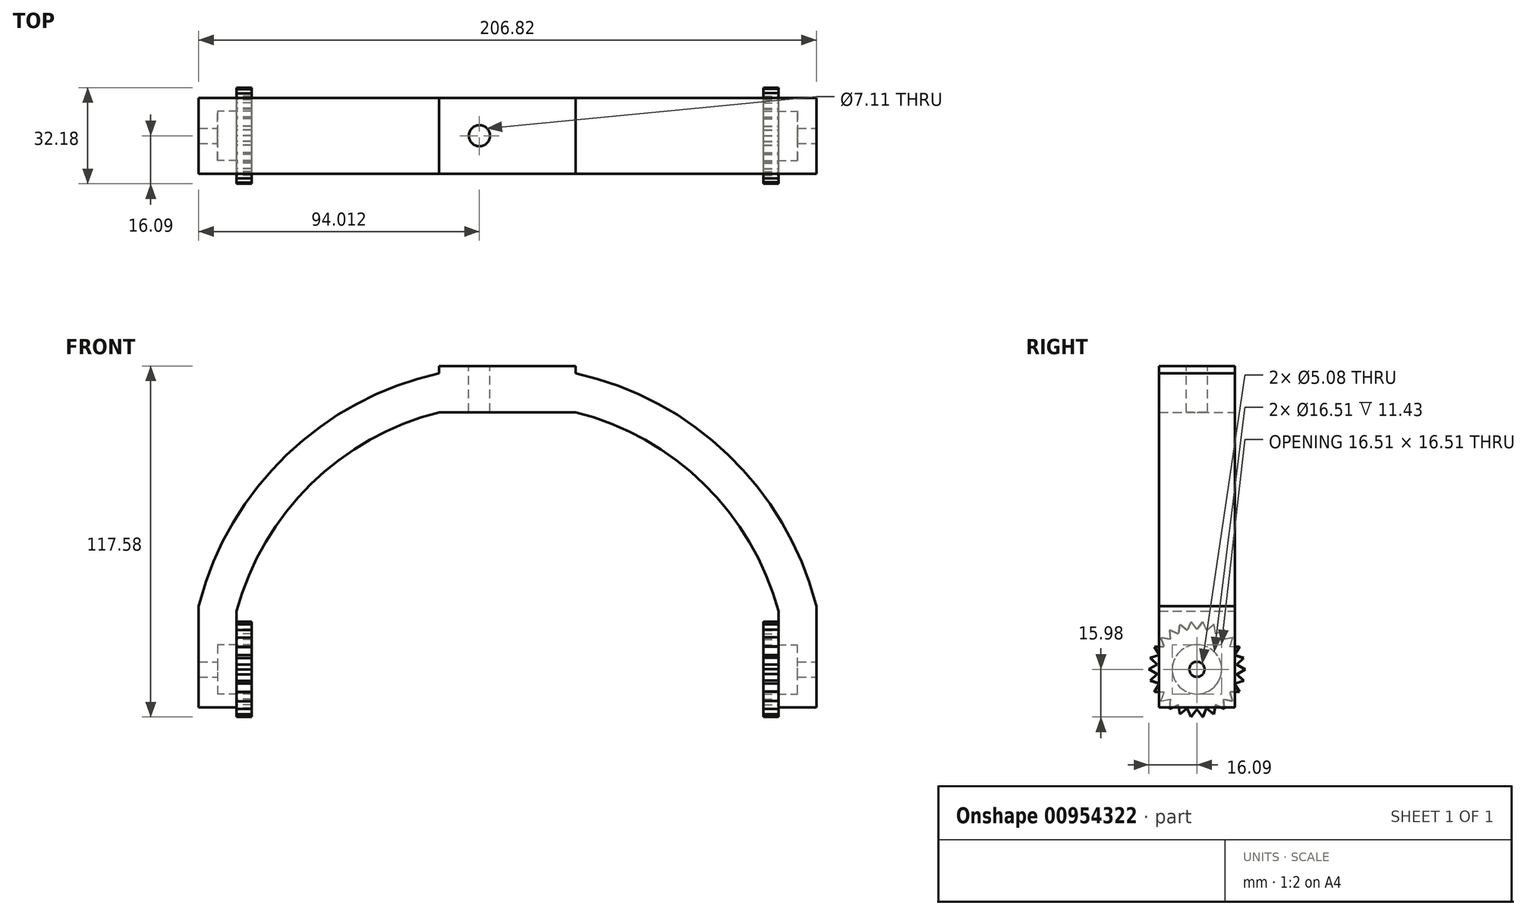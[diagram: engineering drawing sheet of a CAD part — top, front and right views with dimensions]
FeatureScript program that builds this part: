
annotation { "Feature Type Name" : "Feature", "Feature Type Description" : "" }
export const myFeature = defineFeature(function(context is Context, id is Id, definition is map)
    precondition{}
    {
        {
            var Q0;
            Q0=qCreatedBy(makeId("Front.planeOp"),FACE);
            var sketch = newSketch(context, id + "F0", { "sketchPlane" : qUnion([Q0])});
            skArc(sketch, "E0", {"start": v(97.06, 33.02) * mm, "mid": v(0, 107.95) * mm, "end": v(-97.06, 33.02) * mm});
            skLineSegment(sketch, "E1", {"start": v(-97.06, 33.02) * mm, "end": v(-97.06, 0) * mm});
            skLineSegment(sketch, "E2", {"start": v(97.06, 33.02) * mm, "end": v(97.06, 0) * mm});
            skSolve(sketch);
        }
        {
            var Q0;
            Q0=qCreatedBy(makeId("Top.planeOp"),FACE);
            var sketch = newSketch(context, id + "F1", { "sketchPlane" : qUnion([Q0])});
            skPoint(sketch, "E3.0", {"position": v(-97.06, 0) * mm});
            skLineSegment(sketch, "E4.bottom", {"start": v(-103.41, 12.7) * mm, "end": v(-90.71, 12.7) * mm});
            skLineSegment(sketch, "E4.top", {"start": v(-103.41, -12.7) * mm, "end": v(-90.71, -12.7) * mm});
            skLineSegment(sketch, "E4.left", {"start": v(-103.41, 12.7) * mm, "end": v(-103.41, -12.7) * mm});
            skLineSegment(sketch, "E4.right", {"start": v(-90.71, 12.7) * mm, "end": v(-90.71, -12.7) * mm});
            skSolve(sketch);
        }
        {
            var Q0;
            Q0=qSketchRegion(id+"F1",true);
            var Q1;
            Q1=qConstructionFilter(qBodyType(qCreatedBy(id+"F0",EDGE),BodyType.WIRE),ConstructionObject.NO);
            sweep(context, id + "F2", {"profiles" : qUnion([Q0]), "path" : qUnion([Q1])});
        }
        {
            var Q0;
            Q0=qCreatedBy(makeId("Right.planeOp"),FACE);
            var sketch = newSketch(context, id + "F3", { "sketchPlane" : qUnion([Q0])});
            skCircle(sketch, "E5", {"center": v(0, 12.7) * mm, "radius": 2.54 * mm});
            skSolve(sketch);
        }
        {
            var Q0;
            Q0=qSketchRegion(id+"F3",true);
            extrude(context, id + "F4", {"entities" : qUnion([Q0]), "operationType" : NewBodyOperationType.REMOVE, "endBound" : BoundingType.SYMMETRIC, "oppositeDirection" : true, "depth" : 254 * mm, "offsetDistance" : 25.4 * mm});
        }
        {
            var Q0;
            Q0=makeQuery(id+"F2.opSweep","SWEPT_FACE",FACE,{"disambiguationData":[OSD([sQuery(id+"F0.wireOp",EDGE,"E2"),sQuery(id+"F1.wireOp",EDGE,"E4.left")])]});
            var Q1;
            Q1=makeQuery(id+"F2.opSweep","CAP_VERTEX",VERTEX,{"disambiguationData":[OSD([sQuery(id+"F0.wireOp",EDGE,"E2"),sQuery(id+"F1.wireOp",EDGE,"E4.bottom"),sQuery(id+"F1.wireOp",EDGE,"E4.left")])],"isStart":false});
            cPlane(context, id + "F5", {"entities" : qUnion([Q0, Q1]), "cplaneType" : CPlaneType.PLANE_POINT, "offset" : 25.4 * mm, "width" : 152.4 * mm, "height" : 152.4 * mm});
        }
        {
            var Q0;
            Q0=qCreatedBy(id+"F5.planeOp",FACE);
            var sketch = newSketch(context, id + "F6", { "sketchPlane" : qUnion([Q0])});
            skCircle(sketch, "E6", {"center": v(0, 12.7) * mm, "radius": 5.33 * mm, "construction": true});
            skLineSegment(sketch, "E7.0", {"start": v(-2.67, 17.32) * mm, "end": v(2.67, 17.32) * mm});
            skLineSegment(sketch, "E7.1", {"start": v(2.67, 17.32) * mm, "end": v(5.33, 12.7) * mm});
            skLineSegment(sketch, "E7.2", {"start": v(5.33, 12.7) * mm, "end": v(2.67, 8.08) * mm});
            skLineSegment(sketch, "E7.3", {"start": v(2.67, 8.08) * mm, "end": v(-2.67, 8.08) * mm});
            skLineSegment(sketch, "E7.4", {"start": v(-2.67, 8.08) * mm, "end": v(-5.33, 12.7) * mm});
            skLineSegment(sketch, "E7.5", {"start": v(-5.33, 12.7) * mm, "end": v(-2.67, 17.32) * mm});
            skSolve(sketch);
        }
        {
            var Q0;
            Q0=makeQuery(id+"F2.opSweep","SWEPT_FACE",FACE,{"disambiguationData":[OSD([sQuery(id+"F0.wireOp",EDGE,"E1"),sQuery(id+"F1.wireOp",EDGE,"E4.left")])]});
            var Q1;
            Q1=makeQuery(id+"F2.opSweep","CAP_VERTEX",VERTEX,{"disambiguationData":[OSD([sQuery(id+"F0.wireOp",EDGE,"E1"),sQuery(id+"F1.wireOp",EDGE,"E4.bottom"),sQuery(id+"F1.wireOp",EDGE,"E4.left")])],"isStart":true});
            cPlane(context, id + "F7", {"entities" : qUnion([Q0, Q1]), "cplaneType" : CPlaneType.PLANE_POINT, "offset" : 25.4 * mm, "width" : 152.4 * mm, "height" : 152.4 * mm});
        }
        {
            var Q0;
            Q0=qCreatedBy(id+"F7.planeOp",FACE);
            var sketch = newSketch(context, id + "F8", { "sketchPlane" : qUnion([Q0])});
            skLineSegment(sketch, "E8", {"start": v(0, 0) * mm, "end": v(0, 12.7) * mm, "construction": true});
            skCircle(sketch, "E9", {"center": v(0, 12.7) * mm, "radius": 5.33 * mm, "construction": true});
            skLineSegment(sketch, "E10.0", {"start": v(-2.67, 17.32) * mm, "end": v(2.67, 17.32) * mm});
            skLineSegment(sketch, "E10.1", {"start": v(2.67, 17.32) * mm, "end": v(5.33, 12.7) * mm});
            skLineSegment(sketch, "E10.2", {"start": v(5.33, 12.7) * mm, "end": v(2.67, 8.08) * mm});
            skLineSegment(sketch, "E10.3", {"start": v(2.67, 8.08) * mm, "end": v(-2.67, 8.08) * mm});
            skLineSegment(sketch, "E10.4", {"start": v(-2.67, 8.08) * mm, "end": v(-5.33, 12.7) * mm});
            skLineSegment(sketch, "E10.5", {"start": v(-5.33, 12.7) * mm, "end": v(-2.67, 17.32) * mm});
            skSolve(sketch);
        }
        {
            var Q0;
            Q0=makeQuery(id+"F2.opSweep","SWEPT_FACE",FACE,{"disambiguationData":[OSD([sQuery(id+"F0.wireOp",EDGE,"E1"),sQuery(id+"F1.wireOp",EDGE,"E4.left")])]});
            cPlane(context, id + "F9", {"entities" : qUnion([Q0]), "cplaneType" : CPlaneType.OFFSET, "offset" : 6.35 * mm, "oppositeDirection" : true, "width" : 152.4 * mm, "height" : 152.4 * mm});
        }
        {
            var Q0;
            Q0=qCreatedBy(id+"F9.planeOp",FACE);
            var sketch = newSketch(context, id + "F10", { "sketchPlane" : qUnion([Q0])});
            skLineSegment(sketch, "E11", {"start": v(0, 0) * mm, "end": v(0, 12.7) * mm, "construction": true});
            skCircle(sketch, "E12", {"center": v(0, 12.7) * mm, "radius": 8.26 * mm});
            skSolve(sketch);
        }
        {
            var Q0;
            Q0=makeQuery(id+"F2.opSweep","SWEPT_FACE",FACE,{"disambiguationData":[OSD([sQuery(id+"F0.wireOp",EDGE,"E2"),sQuery(id+"F1.wireOp",EDGE,"E4.left")])]});
            cPlane(context, id + "F11", {"entities" : qUnion([Q0]), "cplaneType" : CPlaneType.OFFSET, "offset" : 6.35 * mm, "oppositeDirection" : true, "width" : 152.4 * mm, "height" : 152.4 * mm});
        }
        {
            var Q0;
            Q0=qCreatedBy(id+"F11.planeOp",FACE);
            var sketch = newSketch(context, id + "F12", { "sketchPlane" : qUnion([Q0])});
            skLineSegment(sketch, "E13", {"start": v(0, 0) * mm, "end": v(0, 12.7) * mm, "construction": true});
            skCircle(sketch, "E14", {"center": v(0, 12.7) * mm, "radius": 8.26 * mm});
            skSolve(sketch);
        }
        {
            var Q0;
            Q0=makeQuery(id+"F2.opSweep","SWEPT_FACE",FACE,{"disambiguationData":[OSD([sQuery(id+"F0.wireOp",EDGE,"E1"),sQuery(id+"F1.wireOp",EDGE,"E4.right")])]});
            var sketch = newSketch(context, id + "F13", { "sketchPlane" : qUnion([Q0])});
            skCircle(sketch, "E15", {"center": v(0, 12.7) * mm, "radius": 13.34 * mm, "construction": true});
            skLineSegment(sketch, "E16", {"start": v(-3.28, 25.63) * mm, "end": v(-2, 28.67) * mm});
            skLineSegment(sketch, "E17", {"start": v(-2, 28.67) * mm, "end": v(0, 26.04) * mm});
            skLineSegment(sketch, "E18.1.0", {"start": v(-6.27, 24.47) * mm, "end": v(-5.76, 27.73) * mm});
            skLineSegment(sketch, "E18.1.1", {"start": v(-5.76, 27.73) * mm, "end": v(-3.2, 25.65) * mm});
            skLineSegment(sketch, "E18.2.0", {"start": v(-8.9, 22.62) * mm, "end": v(-9.18, 25.91) * mm});
            skLineSegment(sketch, "E18.2.1", {"start": v(-9.18, 25.91) * mm, "end": v(-6.2, 24.5) * mm});
            skLineSegment(sketch, "E18.3.0", {"start": v(-11.02, 20.2) * mm, "end": v(-12.08, 23.33) * mm});
            skLineSegment(sketch, "E18.3.1", {"start": v(-12.08, 23.33) * mm, "end": v(-8.84, 22.68) * mm});
            skLineSegment(sketch, "E18.4.0", {"start": v(-12.5, 17.35) * mm, "end": v(-14.27, 20.13) * mm});
            skLineSegment(sketch, "E18.4.1", {"start": v(-14.27, 20.13) * mm, "end": v(-10.97, 20.28) * mm});
            skLineSegment(sketch, "E18.5.0", {"start": v(-13.25, 14.22) * mm, "end": v(-15.64, 16.5) * mm});
            skLineSegment(sketch, "E18.5.1", {"start": v(-15.64, 16.5) * mm, "end": v(-12.47, 17.43) * mm});
            skLineSegment(sketch, "E18.6.0", {"start": v(-13.23, 11) * mm, "end": v(-16.1, 12.65) * mm});
            skLineSegment(sketch, "E18.6.1", {"start": v(-16.1, 12.65) * mm, "end": v(-13.24, 14.3) * mm});
            skLineSegment(sketch, "E18.7.0", {"start": v(-12.44, 7.89) * mm, "end": v(-15.61, 8.8) * mm});
            skLineSegment(sketch, "E18.7.1", {"start": v(-15.61, 8.8) * mm, "end": v(-13.24, 11.1) * mm});
            skLineSegment(sketch, "E18.8.0", {"start": v(-10.92, 5.05) * mm, "end": v(-14.22, 5.17) * mm});
            skLineSegment(sketch, "E18.8.1", {"start": v(-14.22, 5.17) * mm, "end": v(-12.47, 7.97) * mm});
            skLineSegment(sketch, "E18.9.0", {"start": v(-8.78, 2.66) * mm, "end": v(-12, 1.99) * mm});
            skLineSegment(sketch, "E18.9.1", {"start": v(-12, 1.99) * mm, "end": v(-10.97, 5.12) * mm});
            skLineSegment(sketch, "E18.10.0", {"start": v(-6.12, 0.85) * mm, "end": v(-9.1, -0.57) * mm});
            skLineSegment(sketch, "E18.10.1", {"start": v(-9.1, -0.57) * mm, "end": v(-8.84, 2.72) * mm});
            skLineSegment(sketch, "E18.11.0", {"start": v(-3.1, -0.27) * mm, "end": v(-5.66, -2.37) * mm});
            skLineSegment(sketch, "E18.11.1", {"start": v(-5.66, -2.37) * mm, "end": v(-6.2, 0.9) * mm});
            skLineSegment(sketch, "E18.12.0", {"start": v(0.09, -0.63) * mm, "end": v(-1.89, -3.28) * mm});
            skLineSegment(sketch, "E18.12.1", {"start": v(-1.89, -3.28) * mm, "end": v(-3.2, -0.25) * mm});
            skLineSegment(sketch, "E18.13.0", {"start": v(3.28, -0.23) * mm, "end": v(2, -3.27) * mm});
            skLineSegment(sketch, "E18.13.1", {"start": v(2, -3.27) * mm, "end": v(0, -0.63) * mm});
            skLineSegment(sketch, "E18.14.0", {"start": v(6.27, 0.93) * mm, "end": v(5.76, -2.33) * mm});
            skLineSegment(sketch, "E18.14.1", {"start": v(5.76, -2.33) * mm, "end": v(3.2, -0.25) * mm});
            skLineSegment(sketch, "E18.15.0", {"start": v(8.9, 2.78) * mm, "end": v(9.18, -0.51) * mm});
            skLineSegment(sketch, "E18.15.1", {"start": v(9.18, -0.51) * mm, "end": v(6.2, 0.9) * mm});
            skLineSegment(sketch, "E18.16.0", {"start": v(11.02, 5.2) * mm, "end": v(12.08, 2.07) * mm});
            skLineSegment(sketch, "E18.16.1", {"start": v(12.08, 2.07) * mm, "end": v(8.84, 2.72) * mm});
            skLineSegment(sketch, "E18.17.0", {"start": v(12.5, 8.05) * mm, "end": v(14.27, 5.27) * mm});
            skLineSegment(sketch, "E18.17.1", {"start": v(14.27, 5.27) * mm, "end": v(10.97, 5.12) * mm});
            skLineSegment(sketch, "E18.18.0", {"start": v(13.25, 11.18) * mm, "end": v(15.64, 8.9) * mm});
            skLineSegment(sketch, "E18.18.1", {"start": v(15.64, 8.9) * mm, "end": v(12.47, 7.97) * mm});
            skLineSegment(sketch, "E18.19.0", {"start": v(13.23, 14.4) * mm, "end": v(16.1, 12.75) * mm});
            skLineSegment(sketch, "E18.19.1", {"start": v(16.1, 12.75) * mm, "end": v(13.24, 11.1) * mm});
            skLineSegment(sketch, "E18.20.0", {"start": v(12.44, 17.51) * mm, "end": v(15.61, 16.6) * mm});
            skLineSegment(sketch, "E18.20.1", {"start": v(15.61, 16.6) * mm, "end": v(13.24, 14.3) * mm});
            skLineSegment(sketch, "E18.21.0", {"start": v(10.92, 20.35) * mm, "end": v(14.22, 20.23) * mm});
            skLineSegment(sketch, "E18.21.1", {"start": v(14.22, 20.23) * mm, "end": v(12.47, 17.43) * mm});
            skLineSegment(sketch, "E18.22.0", {"start": v(8.78, 22.74) * mm, "end": v(12, 23.41) * mm});
            skLineSegment(sketch, "E18.22.1", {"start": v(12, 23.41) * mm, "end": v(10.97, 20.28) * mm});
            skLineSegment(sketch, "E18.23.0", {"start": v(6.12, 24.55) * mm, "end": v(9.1, 25.97) * mm});
            skLineSegment(sketch, "E18.23.1", {"start": v(9.1, 25.97) * mm, "end": v(8.84, 22.68) * mm});
            skLineSegment(sketch, "E18.24.0", {"start": v(3.1, 25.67) * mm, "end": v(5.66, 27.77) * mm});
            skLineSegment(sketch, "E18.24.1", {"start": v(5.66, 27.77) * mm, "end": v(6.2, 24.5) * mm});
            skLineSegment(sketch, "E18.25.0", {"start": v(-0.09, 26.03) * mm, "end": v(1.89, 28.68) * mm});
            skLineSegment(sketch, "E18.25.1", {"start": v(1.89, 28.68) * mm, "end": v(3.2, 25.65) * mm});
            skSolve(sketch);
        }
        {
            var Q0;
            Q0=qSketchRegion(id+"F13",true);
            extrude(context, id + "F14", {"entities" : qUnion([Q0]), "operationType" : NewBodyOperationType.ADD, "depth" : 5.08 * mm, "offsetDistance" : 25.4 * mm});
        }
        {
            var Q0;
            Q0=makeQuery(id+"F2.opSweep","SWEPT_FACE",FACE,{"disambiguationData":[OSD([sQuery(id+"F0.wireOp",EDGE,"E2"),sQuery(id+"F1.wireOp",EDGE,"E4.right")])]});
            var sketch = newSketch(context, id + "F15", { "sketchPlane" : qUnion([Q0])});
            skCircle(sketch, "E19", {"center": v(0, 12.7) * mm, "radius": 13.34 * mm, "construction": true});
            skLineSegment(sketch, "E20", {"start": v(-3.28, 25.63) * mm, "end": v(-2, 28.67) * mm});
            skLineSegment(sketch, "E21", {"start": v(-2, 28.67) * mm, "end": v(0, 26.04) * mm});
            skLineSegment(sketch, "E22.1.0", {"start": v(-5.76, 27.73) * mm, "end": v(-3.2, 25.65) * mm});
            skLineSegment(sketch, "E22.1.1", {"start": v(-6.27, 24.47) * mm, "end": v(-5.76, 27.73) * mm});
            skLineSegment(sketch, "E22.2.0", {"start": v(-9.18, 25.91) * mm, "end": v(-6.2, 24.5) * mm});
            skLineSegment(sketch, "E22.2.1", {"start": v(-8.9, 22.62) * mm, "end": v(-9.18, 25.91) * mm});
            skLineSegment(sketch, "E22.3.0", {"start": v(-12.08, 23.33) * mm, "end": v(-8.84, 22.68) * mm});
            skLineSegment(sketch, "E22.3.1", {"start": v(-11.02, 20.2) * mm, "end": v(-12.08, 23.33) * mm});
            skLineSegment(sketch, "E22.4.0", {"start": v(-14.27, 20.13) * mm, "end": v(-10.97, 20.28) * mm});
            skLineSegment(sketch, "E22.4.1", {"start": v(-12.5, 17.35) * mm, "end": v(-14.27, 20.13) * mm});
            skLineSegment(sketch, "E22.5.0", {"start": v(-15.64, 16.5) * mm, "end": v(-12.47, 17.43) * mm});
            skLineSegment(sketch, "E22.5.1", {"start": v(-13.25, 14.22) * mm, "end": v(-15.64, 16.5) * mm});
            skLineSegment(sketch, "E22.6.0", {"start": v(-16.1, 12.65) * mm, "end": v(-13.24, 14.3) * mm});
            skLineSegment(sketch, "E22.6.1", {"start": v(-13.23, 11) * mm, "end": v(-16.1, 12.65) * mm});
            skLineSegment(sketch, "E22.7.0", {"start": v(-15.61, 8.8) * mm, "end": v(-13.24, 11.1) * mm});
            skLineSegment(sketch, "E22.7.1", {"start": v(-12.44, 7.89) * mm, "end": v(-15.61, 8.8) * mm});
            skLineSegment(sketch, "E22.8.0", {"start": v(-14.22, 5.17) * mm, "end": v(-12.47, 7.97) * mm});
            skLineSegment(sketch, "E22.8.1", {"start": v(-10.92, 5.05) * mm, "end": v(-14.22, 5.17) * mm});
            skLineSegment(sketch, "E22.9.0", {"start": v(-12, 1.99) * mm, "end": v(-10.97, 5.12) * mm});
            skLineSegment(sketch, "E22.9.1", {"start": v(-8.78, 2.66) * mm, "end": v(-12, 1.99) * mm});
            skLineSegment(sketch, "E22.10.0", {"start": v(-9.1, -0.57) * mm, "end": v(-8.84, 2.72) * mm});
            skLineSegment(sketch, "E22.10.1", {"start": v(-6.12, 0.85) * mm, "end": v(-9.1, -0.57) * mm});
            skLineSegment(sketch, "E22.11.0", {"start": v(-5.66, -2.37) * mm, "end": v(-6.2, 0.9) * mm});
            skLineSegment(sketch, "E22.11.1", {"start": v(-3.1, -0.27) * mm, "end": v(-5.66, -2.37) * mm});
            skLineSegment(sketch, "E22.12.0", {"start": v(-1.89, -3.28) * mm, "end": v(-3.2, -0.25) * mm});
            skLineSegment(sketch, "E22.12.1", {"start": v(0.09, -0.63) * mm, "end": v(-1.89, -3.28) * mm});
            skLineSegment(sketch, "E22.13.0", {"start": v(2, -3.27) * mm, "end": v(0, -0.63) * mm});
            skLineSegment(sketch, "E22.13.1", {"start": v(3.28, -0.23) * mm, "end": v(2, -3.27) * mm});
            skLineSegment(sketch, "E22.14.0", {"start": v(5.76, -2.33) * mm, "end": v(3.2, -0.25) * mm});
            skLineSegment(sketch, "E22.14.1", {"start": v(6.27, 0.93) * mm, "end": v(5.76, -2.33) * mm});
            skLineSegment(sketch, "E22.15.0", {"start": v(9.18, -0.51) * mm, "end": v(6.2, 0.9) * mm});
            skLineSegment(sketch, "E22.15.1", {"start": v(8.9, 2.78) * mm, "end": v(9.18, -0.51) * mm});
            skLineSegment(sketch, "E22.16.0", {"start": v(12.08, 2.07) * mm, "end": v(8.84, 2.72) * mm});
            skLineSegment(sketch, "E22.16.1", {"start": v(11.02, 5.2) * mm, "end": v(12.08, 2.07) * mm});
            skLineSegment(sketch, "E22.17.0", {"start": v(14.27, 5.27) * mm, "end": v(10.97, 5.12) * mm});
            skLineSegment(sketch, "E22.17.1", {"start": v(12.5, 8.05) * mm, "end": v(14.27, 5.27) * mm});
            skLineSegment(sketch, "E22.18.0", {"start": v(15.64, 8.9) * mm, "end": v(12.47, 7.97) * mm});
            skLineSegment(sketch, "E22.18.1", {"start": v(13.25, 11.18) * mm, "end": v(15.64, 8.9) * mm});
            skLineSegment(sketch, "E22.19.0", {"start": v(16.1, 12.75) * mm, "end": v(13.24, 11.1) * mm});
            skLineSegment(sketch, "E22.19.1", {"start": v(13.23, 14.4) * mm, "end": v(16.1, 12.75) * mm});
            skLineSegment(sketch, "E22.20.0", {"start": v(15.61, 16.6) * mm, "end": v(13.24, 14.3) * mm});
            skLineSegment(sketch, "E22.20.1", {"start": v(12.44, 17.51) * mm, "end": v(15.61, 16.6) * mm});
            skLineSegment(sketch, "E22.21.0", {"start": v(14.22, 20.23) * mm, "end": v(12.47, 17.43) * mm});
            skLineSegment(sketch, "E22.21.1", {"start": v(10.92, 20.35) * mm, "end": v(14.22, 20.23) * mm});
            skLineSegment(sketch, "E22.22.0", {"start": v(12, 23.41) * mm, "end": v(10.97, 20.28) * mm});
            skLineSegment(sketch, "E22.22.1", {"start": v(8.78, 22.74) * mm, "end": v(12, 23.41) * mm});
            skLineSegment(sketch, "E22.23.0", {"start": v(9.1, 25.97) * mm, "end": v(8.84, 22.68) * mm});
            skLineSegment(sketch, "E22.23.1", {"start": v(6.12, 24.55) * mm, "end": v(9.1, 25.97) * mm});
            skLineSegment(sketch, "E22.24.0", {"start": v(5.66, 27.77) * mm, "end": v(6.2, 24.5) * mm});
            skLineSegment(sketch, "E22.24.1", {"start": v(3.1, 25.67) * mm, "end": v(5.66, 27.77) * mm});
            skLineSegment(sketch, "E22.25.0", {"start": v(1.89, 28.68) * mm, "end": v(3.2, 25.65) * mm});
            skLineSegment(sketch, "E22.25.1", {"start": v(-0.09, 26.03) * mm, "end": v(1.89, 28.68) * mm});
            skSolve(sketch);
        }
        {
            var Q0;
            Q0=qSketchRegion(id+"F15",true);
            var Q1;
            Q1=makeQuery(id+"F2.opSweep","SWEPT_FACE",FACE,{"disambiguationData":[OSD([sQuery(id+"F0.wireOp",EDGE,"E2"),sQuery(id+"F1.wireOp",EDGE,"E4.left")])]});
            extrude(context, id + "F16", {"entities" : qUnion([Q0, Q1]), "operationType" : NewBodyOperationType.ADD, "depth" : 5.08 * mm, "offsetDistance" : 25.4 * mm});
        }
        {
            var Q0;
            Q0=qSketchRegion(id+"F10",true);
            extrude(context, id + "F17", {"entities" : qUnion([Q0]), "operationType" : NewBodyOperationType.REMOVE, "oppositeDirection" : true, "depth" : 63.75 * mm, "offsetDistance" : 25.4 * mm});
        }
        {
            var Q0;
            Q0=qSketchRegion(id+"F12",true);
            extrude(context, id + "F18", {"entities" : qUnion([Q0]), "operationType" : NewBodyOperationType.REMOVE, "oppositeDirection" : true, "depth" : 25.4 * mm, "offsetDistance" : 25.4 * mm});
        }
        {
            var Q0;
            Q0=makeQuery(id+"F2.opSweep","SWEPT_EDGE",EDGE,{"disambiguationData":[OSD([sQuery(id+"F0.wireOp",EDGE,"E0"),sQuery(id+"F1.wireOp",EDGE,"E4.top"),sQuery(id+"F1.wireOp",EDGE,"E4.left")]),OD(2.0)]});
            cPoint(context, id + "F19", {"entities" : qUnion([Q0]), "parameter" : 0.5});
        }
        {
            var Q0;
            Q0=qCreatedBy(makeId("Top.planeOp"),FACE);
            var Q1;
            Q1=qCreatedBy(id+"F19",VERTEX);
            cPlane(context, id + "F20", {"entities" : qUnion([Q0, Q1]), "cplaneType" : CPlaneType.PLANE_POINT, "offset" : 25.4 * mm, "width" : 152.4 * mm, "height" : 152.4 * mm});
        }
        {
            var Q0;
            Q0=qCreatedBy(id+"F20.planeOp",FACE);
            var sketch = newSketch(context, id + "F21", { "sketchPlane" : qUnion([Q0])});
            skFitSpline(sketch, "E23.0", {"points": [v(-103.2, 12.7) * mm, v(-34.4, 12.7) * mm, v(34.4, 12.7) * mm, v(103.2, 12.7) * mm]});
            skLineSegment(sketch, "E24.bottom", {"start": v(-22.86, 12.7) * mm, "end": v(22.86, 12.7) * mm});
            skLineSegment(sketch, "E24.top", {"start": v(-22.86, -12.7) * mm, "end": v(22.86, -12.7) * mm});
            skLineSegment(sketch, "E24.left", {"start": v(-22.86, 12.7) * mm, "end": v(-22.86, -12.7) * mm});
            skLineSegment(sketch, "E24.right", {"start": v(22.86, 12.7) * mm, "end": v(22.86, -12.7) * mm});
            skPoint(sketch, "E24.middle", {"position": v(0, 0) * mm});
            skSolve(sketch);
        }
        {
            var Q0;
            Q0=qSketchRegion(id+"F21",true);
            extrude(context, id + "F22", {"entities" : qUnion([Q0]), "operationType" : NewBodyOperationType.ADD, "oppositeDirection" : true, "depth" : 15.5 * mm, "offsetDistance" : 25.4 * mm});
        }
        {
            var Q0;
            Q0=qCreatedBy(id+"F20.planeOp",FACE);
            var sketch = newSketch(context, id + "F23", { "sketchPlane" : qUnion([Q0])});
            skCircle(sketch, "E25", {"center": v(-9.4, 0) * mm, "radius": 3.56 * mm});
            skCircle(sketch, "E26.MirrorC", {"center": v(9.4, 0) * mm, "radius": 3.56 * mm});
            skSolve(sketch);
        }
        {
            var Q0;
            Q0=makeQuery(id+"F23.imprint","IMPRINT",FACE,{"disambiguationData":[TD([[makeQuery(id+"F23.imprint","IMPRINT",EDGE,{"derivedFrom":sQuery(id+"F23.wireOp",EDGE,"E25")}),1.0]])]});
            var Q1;
            Q1=makeQuery(id+"F23.imprint","IMPRINT",FACE,{"disambiguationData":[TD([[makeQuery(id+"F23.imprint","IMPRINT",EDGE,{"derivedFrom":sQuery(id+"F23.wireOp",EDGE,"E26.MirrorC")}),-1.0]])]});
            extrude(context, id + "F24", {"entities" : qUnion([Q0, Q1]), "operationType" : NewBodyOperationType.REMOVE, "oppositeDirection" : true, "depth" : 25.4 * mm, "offsetDistance" : 25.4 * mm});
        }
    });
